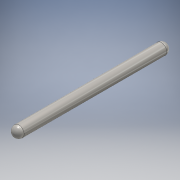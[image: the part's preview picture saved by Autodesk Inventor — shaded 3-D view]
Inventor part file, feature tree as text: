
AUTODESK INVENTOR PART (.ipt)
format: ipt  version: 2016 (Build 200138000, 138)  size: 113,664 bytes
history: native  units: mm
features: fillet x2, extrude x1, sketch x1
ambient origin geometry x8: Origin, YZ Plane, XZ Plane, XY Plane, X Axis, Y Axis, Z Axis, Center Point
bodies: Solid1 (feature_tree)
feature tree (4):
  extrude  "Extrusion1"  Depth=1.0mm TaperAngle=0.0deg
  fillet  "Fillet1"  Radius=1.0mm
  fillet  "Fillet2"  Radius=1.0mm
  sketch  "Sketch1"  dims[d0=2.0mm d1=28.0mm d2=0.0mm d3=1.0mm d4=1.0mm]
